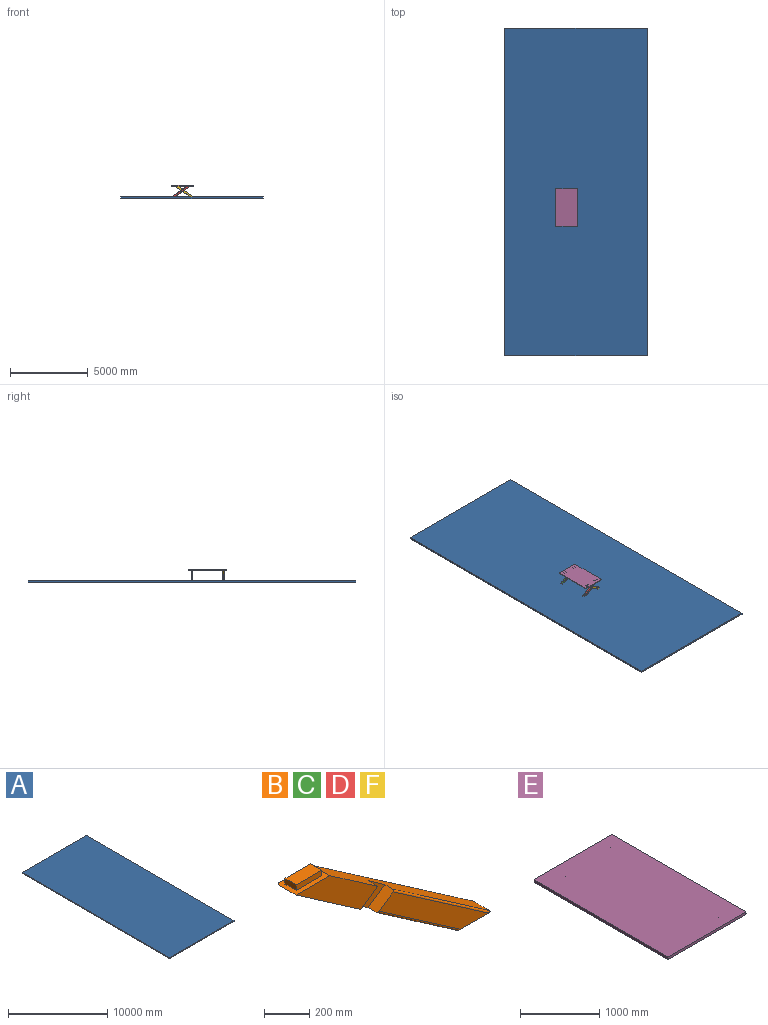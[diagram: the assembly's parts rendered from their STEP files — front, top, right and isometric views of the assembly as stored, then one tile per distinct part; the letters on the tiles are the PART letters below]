
ASSEMBLY  parts=6 mates=7
PART A: 6 faces, bbox 9148.7x21029.5x100 mm
  f0: plane 21029.53x100mm, normal (-1,0,0), area 2102953.1mm2, adj f1,f3,f4,f5
  f1: plane 9148.7x100mm, normal (0,-1,0), area 914869.6mm2, adj f0,f2,f4,f5
  f2: plane 21029.53x100mm, normal (1,0,0), area 2102953.1mm2, adj f1,f3,f4,f5
  f3: plane 9148.7x100mm, normal (0,1,0), area 914869.6mm2, adj f0,f2,f4,f5
  f4: plane 21029.53x9148.7mm, normal (0,0,-1), area 192392789.4mm2, adj f0,f1,f2,f3
  f5: plane 21029.53x9148.7mm, normal (0,0,1), area 192392789.4mm2, adj f0,f1,f2,f3
PART B: 19 faces, bbox 1323.8x120x787.3 mm
  f0: plane 684.42x413.17mm, normal (0,-1,0), area 67229.2mm2, adj f2,f8,f15,f16
  f1: plane 1010.77x700mm, normal (-0.57,0,-0.82), area 121471mm2, adj f2,f4,f6,f7,f8,f9,f15,f17
  f2: plane 210.77x120mm, normal (0,0,-1), area 25175.4mm2, adj f0,f1,f3,f5,f15,f16,f17,f18
  f3: plane 1010.77x700mm, normal (0.57,0,0.82), area 120189.1mm2, adj f2,f4,f6,f7,f8,f9,f16,f18
  f4: plane 210.77x120mm, normal (0,0,1), area 13980mm2, adj f1,f3,f5,f6,f10,f11,f12,f13
  f5: plane 1186.41x700mm, normal (0,1,0), area 122949.5mm2, adj f2,f4,f17,f18
  f6: plane 510.77x280.75mm, normal (0,-1,0), area 51481.6mm2, adj f1,f3,f4,f7
  f7: plane 105.39x72.98mm, normal (0.57,0,-0.82), area 7691.4mm2, adj f1,f3,f6,f9
  f8: plane 105.39x72.98mm, normal (-0.57,0,0.82), area 7655.8mm2, adj f0,f1,f3,f9,f15,f16
  f9: plane 210.77x145.97mm, normal (0,-1,0), area 15382.8mm2, adj f1,f3,f7,f8
  f10: plane 70x30mm, normal (1,0,0), area 2100mm2, adj f4,f11,f13,f14
  f11: plane 160.77x30mm, normal (0,1,0), area 4823.1mm2, adj f4,f10,f12,f14
  f12: plane 70x30mm, normal (-1,0,0), area 2100mm2, adj f4,f11,f13,f14
  f13: plane 160.77x30mm, normal (0,-1,0), area 4823.1mm2, adj f4,f10,f12,f14
  f14: plane 160.77x70mm, normal (0,0,1), area 11253.9mm2, adj f10,f11,f12,f13
  f15: bspline ~568.75x398.16mm, area 9931.6mm2, adj f0,f1,f2,f8
  f16: bspline ~675.01x471.75mm, area 11894mm2, adj f0,f2,f3,f8
  f17: bspline ~1130.6x787.26mm, area 19957.5mm2, adj f1,f2,f4,f5
  f18: bspline ~1130.6x787.26mm, area 19957.5mm2, adj f2,f3,f4,f5
PART C: same geometry as B
PART D: same geometry as B
PART E: 30 faces, bbox 1400x2400x44 mm
  f0: plane 1380x40mm, normal (0,1,0), area 55200mm2, adj f6,f8,f28,f29
  f1: plane 2380x40mm, normal (-1,0,0), area 95200mm2, adj f6,f8,f27,f29
  f2: plane 160.77x30mm, normal (0,-1,0), area 4823.1mm2, adj f3,f5,f6,f7
  f3: plane 70x30mm, normal (-1,0,0), area 2100mm2, adj f2,f4,f6,f7
  f4: plane 160.77x30mm, normal (0,1,0), area 4823.1mm2, adj f3,f5,f6,f7
  f5: plane 70x30mm, normal (1,0,0), area 2100mm2, adj f2,f4,f6,f7
  f6: plane 2400x1400mm, normal (0,0,-1), area 3314917.6mm2, adj f0,f1,f2,f3,f4,f5,f9,f10
  f7: plane 160.77x70mm, normal (0,0,-1), area 11253.9mm2, adj f2,f3,f4,f5
  f8: plane 2400x1400mm, normal (0,0,1), area 3359933.3mm2, adj f0,f1,f9,f15,f26,f27,f28,f29
  f9: plane 2380x40mm, normal (1,0,0), area 95200mm2, adj f6,f8,f26,f28
  f10: plane 160.77x30mm, normal (0,-1,0), area 4823.1mm2, adj f6,f11,f13,f14
  f11: plane 70x30mm, normal (1,0,0), area 2100mm2, adj f6,f10,f12,f14
  f12: plane 160.77x30mm, normal (0,1,0), area 4823.1mm2, adj f6,f11,f13,f14
  f13: plane 70x30mm, normal (-1,0,0), area 2100mm2, adj f6,f10,f12,f14
  f14: plane 160.77x70mm, normal (0,0,-1), area 11253.9mm2, adj f10,f11,f12,f13
  f15: plane 1380x40mm, normal (0,-1,0), area 55200mm2, adj f6,f8,f26,f27
  f16: plane 160.77x30mm, normal (0,1,0), area 4823.1mm2, adj f6,f17,f19,f20
  f17: plane 70x30mm, normal (-1,0,0), area 2100mm2, adj f6,f16,f18,f20
  f18: plane 160.77x30mm, normal (0,-1,0), area 4823.1mm2, adj f6,f17,f19,f20
  f19: plane 70x30mm, normal (1,0,0), area 2100mm2, adj f6,f16,f18,f20
  f20: plane 160.77x70mm, normal (0,0,-1), area 11253.9mm2, adj f16,f17,f18,f19
  f21: plane 160.77x30mm, normal (0,1,0), area 4823.1mm2, adj f6,f22,f24,f25
  f22: plane 70x30mm, normal (1,0,0), area 2100mm2, adj f6,f21,f23,f25
  f23: plane 160.77x30mm, normal (0,-1,0), area 4823.1mm2, adj f6,f22,f24,f25
  f24: plane 70x30mm, normal (-1,0,0), area 2100mm2, adj f6,f21,f23,f25
  f25: plane 160.77x70mm, normal (0,0,-1), area 11253.9mm2, adj f21,f22,f23,f24
  f26: bspline ~44x10mm, area 649.3mm2, adj f6,f8,f9,f15
  f27: bspline ~44x10mm, area 649.3mm2, adj f1,f6,f8,f15
  f28: bspline ~44x10mm, area 649.3mm2, adj f0,f6,f8,f9
  f29: bspline ~44x10mm, area 649.3mm2, adj f0,f1,f6,f8
PART F: same geometry as B
PLACE A t=(-196.62,286.95,601.97)mm
PLACE B t=(-302.01,226.95,601.97)mm
PLACE C rot(axis=(0,0,1),180deg) t=(-1302.01,346.95,601.97)mm
PLACE D rot(axis=(0,0,1),180deg) t=(-1302.01,-1653.05,601.97)mm
PLACE E t=(-302.01,226.95,601.97)mm
PLACE F t=(-302.01,-1773.05,601.97)mm
MATE fastened D.f9 <-> F.f9  axis (0,1,0) through (-802.01,-1713.05,1021.23)mm
MATE fastened B.f2 <-> A.f5  axis (0,0,-1) through (-196.62,286.95,601.97)mm
MATE fastened C.f14 <-> E.f14  axis (0,0,1) through (-396.62,286.95,1331.97)mm
MATE fastened C.f9 <-> B.f9  axis (0,1,0) through (-802.01,286.95,1021.23)mm
MATE fastened F.f14 <-> E.f20  axis (0,0,1) through (-1207.39,-1713.05,1331.97)mm
MATE fastened D.f14 <-> E.f25  axis (0,0,1) through (-396.62,-1713.05,1331.97)mm
MATE fastened B.f14 <-> E.f7  axis (0,0,1) through (-1207.39,286.95,1331.97)mm
